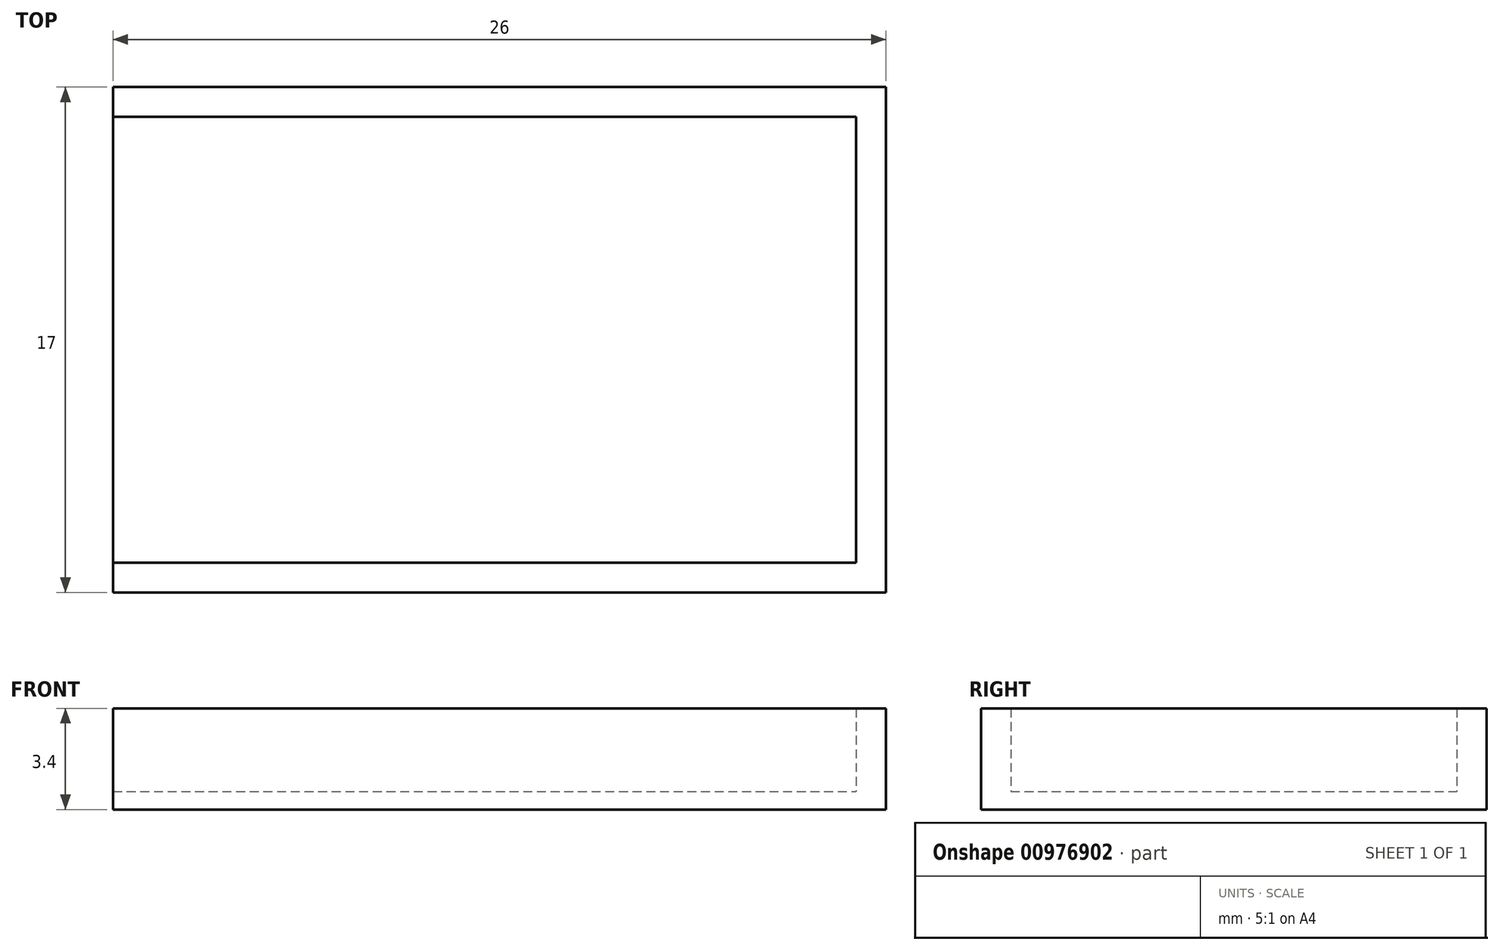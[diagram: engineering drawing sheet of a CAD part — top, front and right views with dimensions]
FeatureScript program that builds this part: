
annotation { "Feature Type Name" : "Feature", "Feature Type Description" : "" }
export const myFeature = defineFeature(function(context is Context, id is Id, definition is map)
    precondition{}
    {
        {
            var Q0;
            Q0=qCreatedBy(makeId("Top.planeOp"),FACE);
            var sketch = newSketch(context, id + "F0", { "sketchPlane" : qUnion([Q0])});
            skLineSegment(sketch, "E0.bottom", {"start": v(0, 0) * mm, "end": v(-26, 0) * mm});
            skLineSegment(sketch, "E0.top", {"start": v(0, 17) * mm, "end": v(-26, 17) * mm});
            skLineSegment(sketch, "E0.left", {"start": v(0, 0) * mm, "end": v(0, 17) * mm});
            skLineSegment(sketch, "E0.right", {"start": v(-26, 0) * mm, "end": v(-26, 17) * mm});
            skSolve(sketch);
        }
        {
            var Q0;
            Q0 = qSketchRegion(id + "F0", true);
            extrude(context, id + "F1", {"entities" : qUnion([Q0]), "depth" : .6 * mm, "offsetDistance" : 25 * mm});
        }
        {
            var Q0;
            Q0=makeQuery(id+"F1.opExtrude","CAP_FACE",FACE,{"disambiguationData":[OSD([sQuery(id+"F0.wireOp",EDGE,"E0.bottom"),sQuery(id+"F0.wireOp",EDGE,"E0.top"),sQuery(id+"F0.wireOp",EDGE,"E0.left"),sQuery(id+"F0.wireOp",EDGE,"E0.right")])],"isStart":false});
            var sketch = newSketch(context, id + "F2", { "sketchPlane" : qUnion([Q0])});
            skLineSegment(sketch, "E1.bottom", {"start": v(-26, 16) * mm, "end": v(-1, 16) * mm});
            skLineSegment(sketch, "E1.top", {"start": v(-26, 1) * mm, "end": v(-1, 1) * mm});
            skLineSegment(sketch, "E1.left", {"start": v(-26, 16) * mm, "end": v(-26, 1) * mm});
            skLineSegment(sketch, "E1.right", {"start": v(-1, 16) * mm, "end": v(-1, 1) * mm});
            skSolve(sketch);
        }
        {
            var Q0;
            {var subQ2=sQuery(id+"F2.wireOp",EDGE,"E1.bottom");Q0=makeQuery(id+"F2.imprint","IMPRINT",FACE,{"disambiguationData":[TD([[makeQuery(id+"F2.imprint","IMPRINT",EDGE,{"derivedFrom":subQ2}),1.0]])]});}
            extrude(context, id + "F3", {"entities" : qUnion([Q0]), "operationType" : NewBodyOperationType.ADD, "depth" : 2.8 * mm, "offsetDistance" : 25 * mm});
        }
    });
